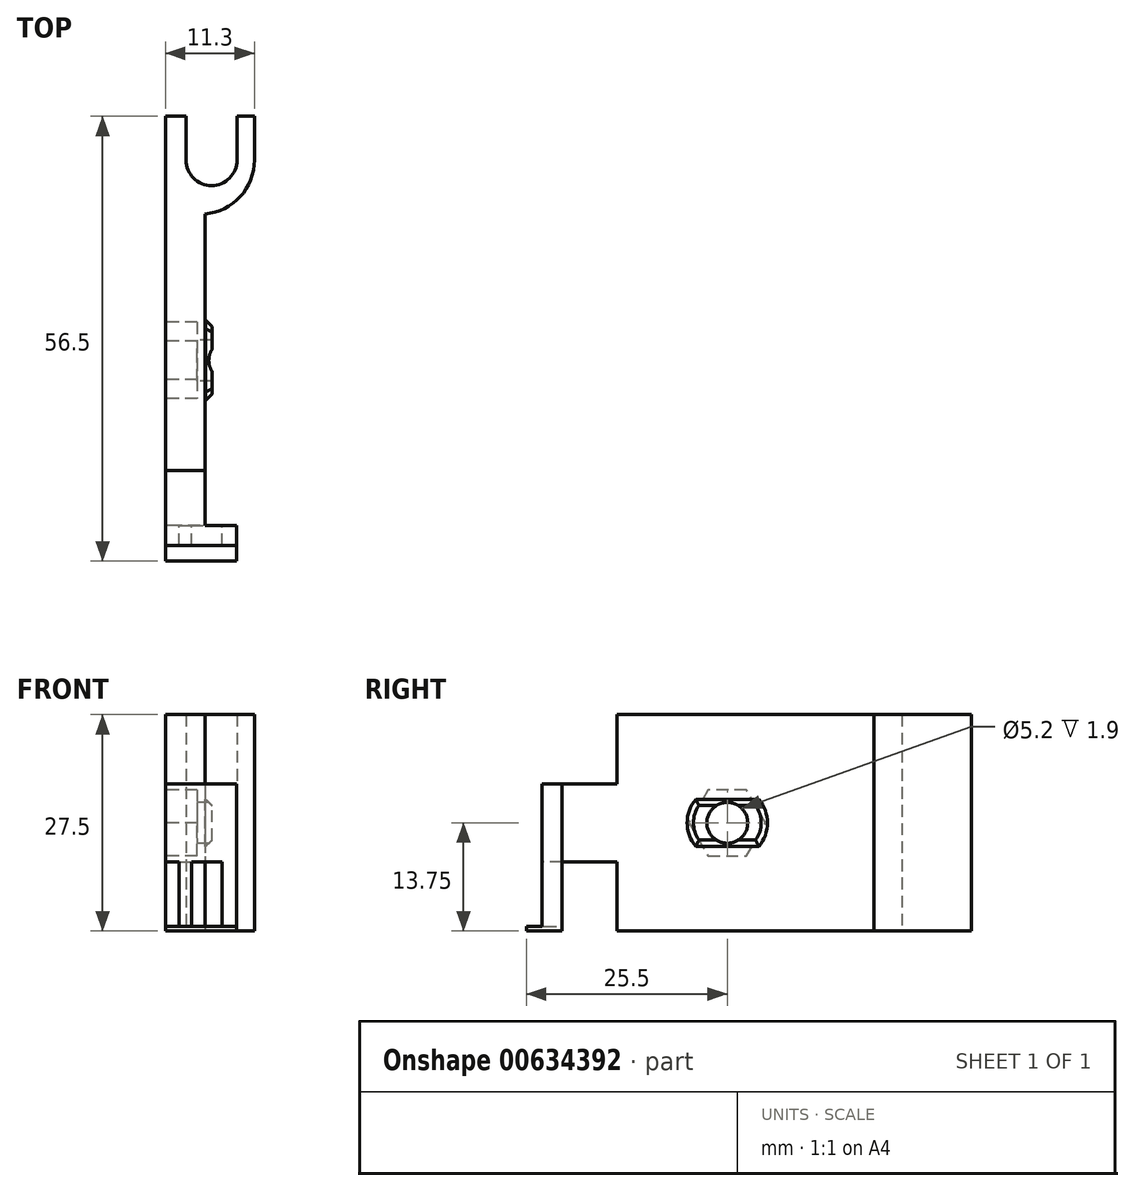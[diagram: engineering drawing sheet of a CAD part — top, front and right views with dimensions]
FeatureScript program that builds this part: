
annotation { "Feature Type Name" : "Feature", "Feature Type Description" : "" }
export const myFeature = defineFeature(function(context is Context, id is Id, definition is map)
    precondition{}
    {
        {
            var Q0;
            Q0=qCreatedBy(makeId("Top.planeOp"),FACE);
            var sketch = newSketch(context, id + "F0", { "sketchPlane" : qUnion([Q0])});
            skLineSegment(sketch, "E0", {"start": v(0, 0) * mm, "end": v(0, -54.5) * mm});
            skLineSegment(sketch, "E1", {"start": v(0, -54.5) * mm, "end": v(5, -54.5) * mm});
            skLineSegment(sketch, "E2", {"start": v(5, -54.5) * mm, "end": v(5, -12.4) * mm});
            skLineSegment(sketch, "E3", {"start": v(0, 0) * mm, "end": v(2.6, 0) * mm});
            skLineSegment(sketch, "E4", {"start": v(2.6, 0) * mm, "end": v(2.6, -5.55) * mm});
            skArc(sketch, "E5", {"start": v(2.6, -5.55) * mm, "mid": v(5.85, -8.8) * mm, "end": v(9.1, -5.55) * mm});
            skLineSegment(sketch, "E6", {"start": v(9.1, -5.55) * mm, "end": v(9.1, 0) * mm});
            skPoint(sketch, "E6.endSnap0", {"position": v(1.3, 0) * mm});
            skLineSegment(sketch, "E7", {"start": v(9.1, 0) * mm, "end": v(11.3, 0) * mm});
            skLineSegment(sketch, "E8", {"start": v(11.3, 0) * mm, "end": v(11.3, -5.55) * mm});
            skArc(sketch, "E9", {"start": v(5, -12.4) * mm, "mid": v(9.49, -10.2) * mm, "end": v(11.3, -5.55) * mm});
            skSolve(sketch);
        }
        {
            var Q0;
            Q0=makeQuery(id+"F0.imprint","IMPRINT",FACE,{"disambiguationData":[TD([[makeQuery(id+"F0.imprint","IMPRINT",EDGE,{"derivedFrom":sQuery(id+"F0.wireOp",EDGE,"E0")}),1.0]])]});
            extrude(context, id + "F1", {"entities" : qUnion([Q0]), "depth" : 27.5 * mm, "offsetDistance" : 25 * mm, "symmetric" : true});
        }
        {
            var Q0;
            Q0=makeQuery(id+"F1.opExtrude","SWEPT_FACE",FACE,{"disambiguationData":[OSD([sQuery(id+"F0.wireOp",EDGE,"E2")])]});
            var sketch = newSketch(context, id + "F2", { "sketchPlane" : qUnion([Q0])});
            skLineSegment(sketch, "E10.bottom", {"start": v(-52, 4.95) * mm, "end": v(-54.5, 4.95) * mm});
            skLineSegment(sketch, "E10.top", {"start": v(-52, -4.95) * mm, "end": v(-54.5, -4.95) * mm});
            skLineSegment(sketch, "E10.left", {"start": v(-52, 4.95) * mm, "end": v(-52, -4.95) * mm});
            skLineSegment(sketch, "E10.right", {"start": v(-54.5, 4.95) * mm, "end": v(-54.5, -4.95) * mm});
            skLineSegment(sketch, "E11", {"start": v(-54.5, 0) * mm, "end": v(-52, 0) * mm, "construction": true});
            skSolve(sketch);
        }
        {
            var Q0;
            Q0=makeQuery(id+"F2.imprint","IMPRINT",FACE,{"disambiguationData":[TD([[makeQuery(id+"F2.imprint","IMPRINT",EDGE,{"derivedFrom":sQuery(id+"F2.wireOp",EDGE,"E10.bottom")}),1.0]])]});
            extrude(context, id + "F3", {"entities" : qUnion([Q0]), "operationType" : NewBodyOperationType.ADD, "depth" : 4 * mm, "offsetDistance" : 25 * mm});
        }
        {
            var Q0;
            Q0=makeQuery(id+"F1.opExtrude","SWEPT_FACE",FACE,{"disambiguationData":[OSD([sQuery(id+"F0.wireOp",EDGE,"E0")])]});
            var sketch = newSketch(context, id + "F4", { "sketchPlane" : qUnion([Q0])});
            skCircle(sketch, "E12.cCircle", {"center": v(31, 0) * mm, "radius": 4.2 * mm, "construction": true});
            skLineSegment(sketch, "E12.0", {"start": v(33.42, 4.2) * mm, "end": v(35.85, 0) * mm});
            skLineSegment(sketch, "E12.1", {"start": v(35.85, 0) * mm, "end": v(33.42, -4.2) * mm});
            skLineSegment(sketch, "E12.2", {"start": v(33.42, -4.2) * mm, "end": v(28.58, -4.2) * mm});
            skLineSegment(sketch, "E12.3", {"start": v(28.58, -4.2) * mm, "end": v(26.15, 0) * mm});
            skLineSegment(sketch, "E12.4", {"start": v(26.15, 0) * mm, "end": v(28.58, 4.2) * mm});
            skLineSegment(sketch, "E12.5", {"start": v(28.58, 4.2) * mm, "end": v(33.42, 4.2) * mm});
            skPoint(sketch, "E12.0.midPoint", {"position": v(34.64, 2.1) * mm});
            skCircle(sketch, "E13", {"center": v(31, 0) * mm, "radius": 2.6 * mm});
            skSolve(sketch);
        }
        {
            var Q0;
            Q0 = qSketchRegion(id + "F4", true);
            var Q1;
            Q1=makeQuery(id+"F4.imprint","IMPRINT",FACE,{"disambiguationData":[TD([[makeQuery(id+"F4.imprint","IMPRINT",EDGE,{"derivedFrom":sQuery(id+"F4.wireOp",EDGE,"E13")}),1.0]])]});
            extrude(context, id + "F5", {"entities" : qUnion([Q0, Q1]), "operationType" : NewBodyOperationType.REMOVE, "oppositeDirection" : true, "depth" : 4 * mm, "offsetDistance" : 25 * mm});
        }
        {
            var Q0;
            Q0=makeQuery(id+"F4.imprint","IMPRINT",FACE,{"disambiguationData":[TD([[makeQuery(id+"F4.imprint","IMPRINT",EDGE,{"derivedFrom":sQuery(id+"F4.wireOp",EDGE,"E13")}),1.0]])]});
            extrude(context, id + "F6", {"entities" : qUnion([Q0]), "operationType" : NewBodyOperationType.REMOVE, "endBound" : BoundingType.THROUGH_ALL, "oppositeDirection" : true, "depth" : 25 * mm, "offsetDistance" : 25 * mm});
        }
        {
            var Q0;
            Q0=makeQuery(id+"F1.opExtrude","SWEPT_FACE",FACE,{"disambiguationData":[OSD([sQuery(id+"F0.wireOp",EDGE,"E2")])]});
            var sketch = newSketch(context, id + "F7", { "sketchPlane" : qUnion([Q0])});
            skCircle(sketch, "E14.0", {"center": v(-31, 0) * mm, "radius": 2.6 * mm});
            skLineSegment(sketch, "E15.bottom", {"start": v(-27, -3) * mm, "end": v(-35, -3) * mm});
            skLineSegment(sketch, "E15.top", {"start": v(-27, 3) * mm, "end": v(-35, 3) * mm});
            skLineSegment(sketch, "E15.left", {"start": v(-27, -3) * mm, "end": v(-27, 3) * mm});
            skLineSegment(sketch, "E15.right", {"start": v(-35, -3) * mm, "end": v(-35, 3) * mm});
            skLineSegment(sketch, "E16", {"start": v(-27, 0) * mm, "end": v(-35, 0) * mm, "construction": true});
            skArc(sketch, "E17", {"start": v(-27, -3) * mm, "mid": v(-25.9, 0) * mm, "end": v(-27, 3) * mm});
            skArc(sketch, "E18", {"start": v(-35, 3) * mm, "mid": v(-36.1, 0) * mm, "end": v(-35, -3) * mm});
            skSolve(sketch);
        }
        {
            var Q0;
            Q0=makeQuery(id+"F7.imprint","IMPRINT",FACE,{"disambiguationData":[TD([[makeQuery(id+"F7.imprint","IMPRINT",EDGE,{"derivedFrom":sQuery(id+"F7.wireOp",EDGE,"E15.left")}),-1.0]])]});
            var Q1;
            Q1=makeQuery(id+"F7.imprint","IMPRINT",FACE,{"disambiguationData":[TD([[makeQuery(id+"F7.imprint","IMPRINT",EDGE,{"derivedFrom":sQuery(id+"F7.wireOp",EDGE,"E14.0")}),1.0]])]});
            var Q2;
            Q2=makeQuery(id+"F7.imprint","IMPRINT",FACE,{"disambiguationData":[TD([[makeQuery(id+"F7.imprint","IMPRINT",EDGE,{"derivedFrom":sQuery(id+"F7.wireOp",EDGE,"E15.right")}),1.0]])]});
            extrude(context, id + "F8", {"entities" : qUnion([Q0, Q1, Q2]), "operationType" : NewBodyOperationType.ADD, "depth" : 0.9 * mm, "offsetDistance" : 25 * mm});
        }
        {
            var Q0;
            Q0=makeQuery(id+"F8.opExtrude","CAP_EDGE",EDGE,{"disambiguationData":[OSD([sQuery(id+"F7.wireOp",EDGE,"E15.top")])],"isStart":false});
            var Q1;
            Q1=makeQuery(id+"F8.opExtrude","CAP_EDGE",EDGE,{"disambiguationData":[OSD([sQuery(id+"F7.wireOp",EDGE,"E15.bottom")])],"isStart":false});
            chamfer(context, id + "F9", {"entities" : qUnion([Q0, Q1]), "width" : 0.8 * mm, "tangentPropagation" : true});
        }
        {
            var Q0;
            Q0=makeQuery(id+"F8.opExtrude","CAP_EDGE",EDGE,{"disambiguationData":[OSD([sQuery(id+"F7.wireOp",EDGE,"E17")])],"isStart":false});
            var Q1;
            Q1=makeQuery(id+"F8.opExtrude","CAP_EDGE",EDGE,{"disambiguationData":[OSD([sQuery(id+"F7.wireOp",EDGE,"E18")])],"isStart":false});
            chamfer(context, id + "F10", {"entities" : qUnion([Q0, Q1]), "width" : 0.8 * mm, "tangentPropagation" : true});
        }
        {
            var Q0;
            Q0=makeQuery(id+"F1.opExtrude","SWEPT_FACE",FACE,{"disambiguationData":[OSD([sQuery(id+"F0.wireOp",EDGE,"E0")])]});
            var sketch = newSketch(context, id + "F11", { "sketchPlane" : qUnion([Q0])});
            skLineSegment(sketch, "E19.0", {"start": v(54.5, 4.95) * mm, "end": v(54.5, -4.95) * mm});
            skLineSegment(sketch, "E20.bottom", {"start": v(54.5, -4.95) * mm, "end": v(45, -4.95) * mm});
            skLineSegment(sketch, "E20.top", {"start": v(54.5, -13.75) * mm, "end": v(45, -13.75) * mm});
            skLineSegment(sketch, "E20.left", {"start": v(54.5, -4.95) * mm, "end": v(54.5, -13.75) * mm});
            skLineSegment(sketch, "E20.right", {"start": v(45, -4.95) * mm, "end": v(45, -13.75) * mm});
            skLineSegment(sketch, "E21.bottom", {"start": v(54.5, 4.95) * mm, "end": v(45, 4.95) * mm});
            skLineSegment(sketch, "E21.top", {"start": v(54.5, 13.75) * mm, "end": v(45, 13.75) * mm});
            skLineSegment(sketch, "E21.left", {"start": v(54.5, 4.95) * mm, "end": v(54.5, 13.75) * mm});
            skLineSegment(sketch, "E21.right", {"start": v(45, 4.95) * mm, "end": v(45, 13.75) * mm});
            skSolve(sketch);
        }
        {
            var Q0;
            Q0=makeQuery(id+"F11.imprint","IMPRINT",FACE,{"disambiguationData":[TD([[makeQuery(id+"F11.imprint","IMPRINT",EDGE,{"derivedFrom":sQuery(id+"F11.wireOp",EDGE,"E21.bottom")}),-1.0]])]});
            var Q1;
            Q1=makeQuery(id+"F11.imprint","IMPRINT",FACE,{"disambiguationData":[TD([[makeQuery(id+"F11.imprint","IMPRINT",EDGE,{"derivedFrom":sQuery(id+"F11.wireOp",EDGE,"E20.bottom")}),1.0]])]});
            extrude(context, id + "F12", {"entities" : qUnion([Q0, Q1]), "operationType" : NewBodyOperationType.REMOVE, "endBound" : BoundingType.THROUGH_ALL, "oppositeDirection" : true, "depth" : 25 * mm, "offsetDistance" : 25 * mm});
        }
        {
            var Q0;
            Q0=makeQuery(id+"F1.opExtrude","CAP_FACE",FACE,{"disambiguationData":[OSD([sQuery(id+"F0.wireOp",EDGE,"E0"),sQuery(id+"F0.wireOp",EDGE,"E1"),sQuery(id+"F0.wireOp",EDGE,"E2"),sQuery(id+"F0.wireOp",EDGE,"E3"),sQuery(id+"F0.wireOp",EDGE,"E4"),sQuery(id+"F0.wireOp",EDGE,"E5"),sQuery(id+"F0.wireOp",EDGE,"E6"),sQuery(id+"F0.wireOp",EDGE,"E7"),sQuery(id+"F0.wireOp",EDGE,"E8"),sQuery(id+"F0.wireOp",EDGE,"E9")])],"isStart":true});
            var sketch = newSketch(context, id + "F13", { "sketchPlane" : qUnion([Q0])});
            skPoint(sketch, "E22.0", {"position": v(5, 52) * mm});
            skPoint(sketch, "E23.0", {"position": v(9, 54.5) * mm});
            skPoint(sketch, "E24.0", {"position": v(0, 54.5) * mm});
            skLineSegment(sketch, "E25.bottom", {"start": v(9, 54.5) * mm, "end": v(7.2, 54.5) * mm});
            skLineSegment(sketch, "E25.top", {"start": v(9, 52) * mm, "end": v(7.2, 52) * mm});
            skLineSegment(sketch, "E25.left", {"start": v(9, 54.5) * mm, "end": v(9, 52) * mm});
            skLineSegment(sketch, "E25.right", {"start": v(7.2, 54.5) * mm, "end": v(7.2, 52) * mm});
            skPoint(sketch, "E26.0", {"position": v(9, 52) * mm});
            skLineSegment(sketch, "E27.bottom", {"start": v(5, 52) * mm, "end": v(0, 52) * mm});
            skLineSegment(sketch, "E27.top", {"start": v(5, 54.5) * mm, "end": v(0, 54.5) * mm});
            skLineSegment(sketch, "E27.left", {"start": v(5, 52) * mm, "end": v(5, 54.5) * mm});
            skLineSegment(sketch, "E27.right", {"start": v(0, 52) * mm, "end": v(0, 54.5) * mm});
            skLineSegment(sketch, "E28.bottom", {"start": v(3.3, 54.5) * mm, "end": v(1.7, 54.5) * mm});
            skLineSegment(sketch, "E28.top", {"start": v(3.3, 52) * mm, "end": v(2.5, 52) * mm});
            skLineSegment(sketch, "E28.left", {"start": v(3.3, 54.5) * mm, "end": v(3.3, 52) * mm});
            skLineSegment(sketch, "E28.right", {"start": v(1.7, 54.5) * mm, "end": v(1.7, 52) * mm});
            skLineSegment(sketch, "E29", {"start": v(3.3, 52) * mm, "end": v(1.7, 54.5) * mm, "construction": true});
            skLineSegment(sketch, "E30", {"start": v(2.5, 52) * mm, "end": v(2.5, 53.25) * mm, "construction": true});
            skLineSegment(sketch, "E31", {"start": v(9, 54.5) * mm, "end": v(9, 56.5) * mm});
            skLineSegment(sketch, "E32", {"start": v(9, 56.5) * mm, "end": v(0, 56.5) * mm});
            skLineSegment(sketch, "E33", {"start": v(0, 56.5) * mm, "end": v(0, 54.5) * mm});
            skLineSegment(sketch, "E34", {"start": v(0, 52) * mm, "end": v(0, 49) * mm});
            skLineSegment(sketch, "E35", {"start": v(0, 49) * mm, "end": v(5, 49) * mm});
            skLineSegment(sketch, "E36", {"start": v(5, 49) * mm, "end": v(5, 52) * mm});
            skLineSegment(sketch, "E37", {"start": v(5, 52) * mm, "end": v(7.2, 52) * mm});
            skSolve(sketch);
        }
        {
            var Q0;
            Q0=makeQuery(id+"F13.imprint","IMPRINT",FACE,{"disambiguationData":[TD([[makeQuery(id+"F13.imprint","IMPRINT",EDGE,{"derivedFrom":sQuery(id+"F13.wireOp",EDGE,"E25.bottom")}),1.0]])]});
            var Q1;
            Q1=makeQuery(id+"F13.imprint","IMPRINT",FACE,{"disambiguationData":[TD([[makeQuery(id+"F13.imprint","IMPRINT",EDGE,{"derivedFrom":sQuery(id+"F13.wireOp",EDGE,"E27.bottom")}),-1.0]])]});
            var Q2;
            Q2=makeQuery(id+"F12.boolean.opBoolean","MERGE",FACE,{"derivedFrom":[makeQuery(id+"F3.opExtrude","SWEPT_FACE",FACE,{"disambiguationData":[OSD([sQuery(id+"F2.wireOp",EDGE,"E10.top")])]})],"fromTools":[makeQuery(id+"F12.opExtrude","SWEPT_FACE",FACE,{"disambiguationData":[OSD([sQuery(id+"F11.wireOp",EDGE,"E20.bottom")])]})]});
            extrude(context, id + "F14", {"entities" : qUnion([Q0, Q1]), "operationType" : NewBodyOperationType.ADD, "endBound" : BoundingType.UP_TO_SURFACE, "oppositeDirection" : true, "depth" : 25 * mm, "endBoundEntityFace" : qUnion([Q2]), "offsetDistance" : 25 * mm});
        }
        {
            var Q0;
            Q0=makeQuery(id+"F13.imprint","IMPRINT",FACE,{"disambiguationData":[TD([[makeQuery(id+"F13.imprint","IMPRINT",EDGE,{"derivedFrom":sQuery(id+"F13.wireOp",EDGE,"E25.bottom")}),-1.0]])]});
            var Q1;
            {var subQ0=sQuery(id+"F13.wireOp",EDGE,"E28.top");Q1=makeQuery(id+"F13.imprint","IMPRINT",FACE,{"disambiguationData":[TD([[makeQuery(id+"F13.imprint","IMPRINT",EDGE,{"derivedFrom":subQ0}),1.0]])]});}
            var Q2;
            {var subQ0=sQuery(id+"F13.wireOp",EDGE,"E27.right");Q2=makeQuery(id+"F13.imprint","IMPRINT",FACE,{"disambiguationData":[TD([[makeQuery(id+"F13.imprint","IMPRINT",EDGE,{"derivedFrom":subQ0}),-1.0]])]});}
            var Q3;
            Q3=makeQuery(id+"F13.imprint","IMPRINT",FACE,{"disambiguationData":[TD([[makeQuery(id+"F13.imprint","IMPRINT",EDGE,{"derivedFrom":sQuery(id+"F13.wireOp",EDGE,"E28.bottom")}),1.0]])]});
            var Q4;
            {var subQ0=sQuery(id+"F13.wireOp",EDGE,"E27.left");Q4=makeQuery(id+"F13.imprint","IMPRINT",FACE,{"disambiguationData":[TD([[makeQuery(id+"F13.imprint","IMPRINT",EDGE,{"derivedFrom":subQ0}),1.0]])]});}
            extrude(context, id + "F15", {"entities" : qUnion([Q0, Q1, Q2, Q3, Q4]), "operationType" : NewBodyOperationType.ADD, "oppositeDirection" : true, "depth" : 0.6 * mm, "offsetDistance" : 25 * mm});
        }
    });
